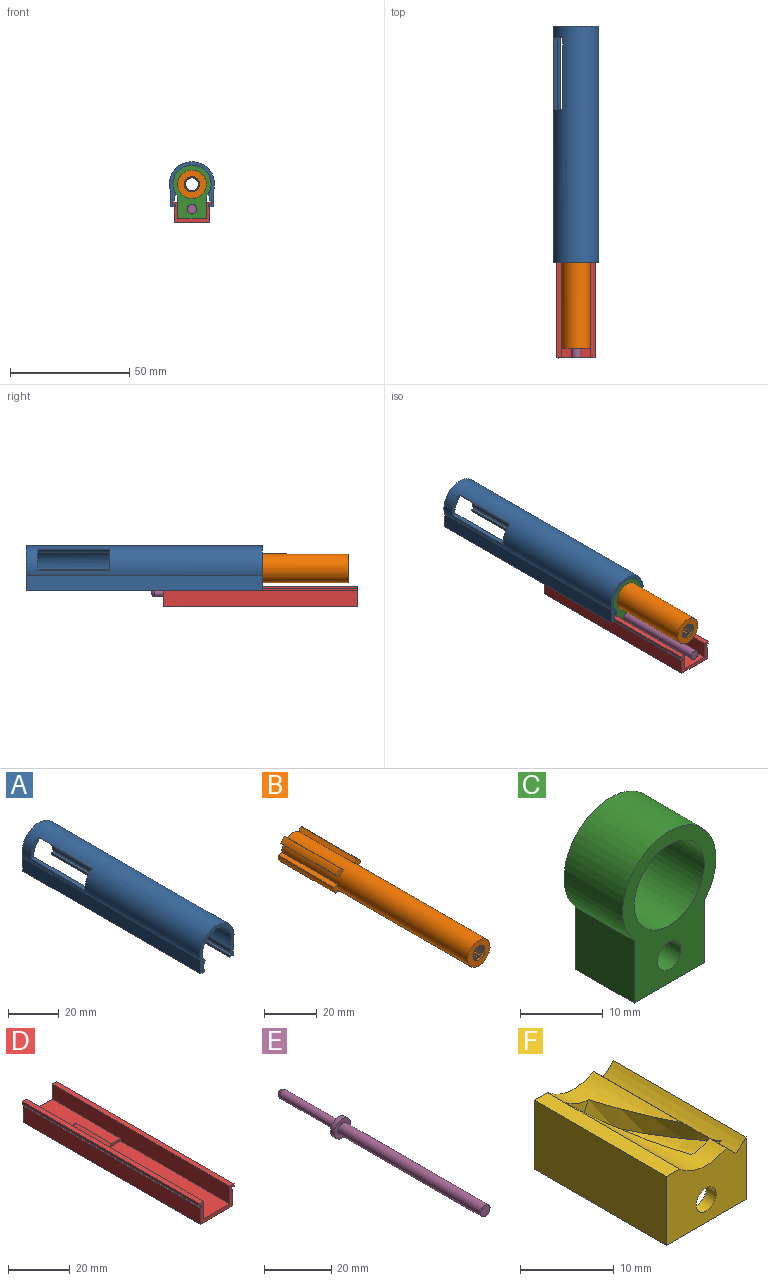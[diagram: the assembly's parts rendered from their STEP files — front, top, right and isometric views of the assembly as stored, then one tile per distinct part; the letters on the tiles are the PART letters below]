
ASSEMBLY  parts=6 mates=6
PART A: 42 faces, bbox 19x99x18.9 mm
  f0: plane 4.17x4.17mm, normal (0,1,0), area 8.4mm2, adj f13,f14,f15,f16
  f1: plane 4.97x2.8mm, normal (0,1,0), area 8.4mm2, adj f16,f17,f18,f19
  f2: plane 12.14x6.49mm, normal (0,1,0), area 30.4mm2, adj f7,f8,f9,f10,f11,f12,f16,f28
  f3: plane 4.97x2.8mm, normal (0,-1,0), area 8.4mm2, adj f7,f8,f9,f16
  f4: plane 4.17x4.17mm, normal (0,-1,0), area 8.4mm2, adj f10,f11,f12,f16
  f5: plane 4.17x4.17mm, normal (0,-1,0), area 8.4mm2, adj f13,f14,f15,f16
  f6: plane 99x1.35mm, normal (0.84,0,-0.54), area 159.4mm2, adj f7,f16,f35,f37,f41
  f7: plane 54x1.45mm, normal (0.71,0,-0.71), area 110.8mm2, adj f2,f3,f6,f8
  f8: cylinder r=5.98mm len=54mm, axis (0,1,0), area 168.9mm2, adj f2,f3,f7,f9
  f9: plane 54x1.98mm, normal (0.26,0,0.97), area 110.8mm2, adj f2,f3,f8,f16
  f10: plane 54x1.98mm, normal (-0.26,0,-0.97), area 110.8mm2, adj f2,f4,f11,f16
  f11: cylinder r=5.98mm len=54mm, axis (0,1,0), area 168.9mm2, adj f2,f4,f10,f12
  f12: plane 54x1.98mm, normal (0.97,0,0.26), area 110.8mm2, adj f2,f4,f11,f16
  f13: plane 54x1.98mm, normal (-0.97,0,0.26), area 110.8mm2, adj f0,f5,f14,f16
  f14: cylinder r=5.98mm len=54mm, axis (0,1,0), area 168.9mm2, adj f0,f5,f13,f15
  f15: plane 54x1.98mm, normal (0.26,0,-0.97), area 110.8mm2, adj f0,f5,f14,f16
  f16: cylinder r=7.97mm len=99mm, axis (0,1,0), area 2030.3mm2, adj f0,f1,f2,f3,f4,f5,f6,f9
  f17: plane 54x1.98mm, normal (-0.26,0,0.97), area 110.8mm2, adj f1,f16,f18,f36
  f18: cylinder r=5.98mm len=54mm, axis (0,1,0), area 168.9mm2, adj f1,f17,f19,f36
  f19: plane 54x1.45mm, normal (-0.71,0,-0.71), area 110.8mm2, adj f1,f18,f20,f36
  f20: plane 99x1.35mm, normal (-0.84,0,-0.54), area 159.4mm2, adj f16,f19,f21,f37,f41
  f21: plane 99x1.65mm, normal (-1,0,0), area 163.2mm2, adj f20,f22,f37,f41
  f22: plane 99x0.5mm, normal (0,0,-1), area 49.5mm2, adj f21,f23,f37,f41
  f23: plane 99x1mm, normal (-1,0,0), area 99mm2, adj f22,f24,f37,f41
  f24: plane 99x1mm, normal (0,0,1), area 99mm2, adj f23,f25,f37,f41
  f25: plane 99x1mm, normal (-1,0,0), area 99mm2, adj f24,f26,f37,f41
  f26: plane 99x2mm, normal (0,0,-1), area 198mm2, adj f25,f27,f37,f41
  f27: plane 99x6.48mm, normal (1,0,0), area 641.1mm2, adj f26,f28,f37,f41
  f28: cylinder r=9.48mm len=99mm, axis (0,1,0), area 3245.8mm2, adj f2,f27,f29,f37,f38,f39,f40,f41
  f29: plane 99x6.48mm, normal (-1,0,0), area 641.1mm2, adj f28,f30,f37,f41
  f30: plane 99x2mm, normal (0,0,-1), area 198mm2, adj f29,f31,f37,f41
  f31: plane 99x1mm, normal (1,0,0), area 99mm2, adj f30,f32,f37,f41
  f32: plane 99x1mm, normal (0,0,1), area 99mm2, adj f31,f33,f37,f41
  f33: plane 99x1mm, normal (1,0,0), area 99mm2, adj f32,f34,f37,f41
  f34: plane 99x0.5mm, normal (0,0,-1), area 49.5mm2, adj f33,f35,f37,f41
  f35: plane 99x1.65mm, normal (1,0,0), area 163.2mm2, adj f6,f34,f37,f41
  f36: plane 4.97x2.8mm, normal (0,-1,0), area 8.4mm2, adj f16,f17,f18,f19
  f37: plane 18.95x18.91mm, normal (0,-1,0), area 72.1mm2, adj f6,f16,f20,f21,f22,f23,f24,f25
  f38: plane 30x1.08mm, normal (-0.71,0,-0.71), area 45.7mm2, adj f2,f16,f28,f40
  f39: plane 30x1.47mm, normal (-0.26,0,0.97), area 45.7mm2, adj f2,f16,f28,f40
  f40: plane 8.63x5.04mm, normal (0,-1,0), area 13.7mm2, adj f16,f28,f38,f39
  f41: plane 18.95x18.91mm, normal (0,1,0), area 72.1mm2, adj f6,f16,f20,f21,f22,f23,f24,f25
PART B: 124 faces, bbox 15.9x105.5x15 mm
  f0: plane 0.75x0.5mm, normal (0,-1,0), area 0.2mm2, adj f45,f48,f55,f102
  f1: plane 0.75x0.66mm, normal (0,1,0), area 0.2mm2, adj f2,f51,f99,f100
  f2: cylinder r=2.85mm len=73.48mm, axis (0,1,0), area 45.5mm2, adj f1,f3,f99,f100
  f3: plane 0.75x0.43mm, normal (0,-1,0), area 0.2mm2, adj f2,f48,f99,f100
  f4: plane 0.75x0.66mm, normal (0,1,0), area 0.2mm2, adj f5,f51,f96,f97
  f5: cylinder r=2.85mm len=73.48mm, axis (0,1,0), area 45.5mm2, adj f4,f6,f96,f97
  f6: plane 0.77x0.64mm, normal (0,-1,0), area 0.2mm2, adj f5,f48,f96,f97
  f7: plane 0.74x0.46mm, normal (0,1,0), area 0.2mm2, adj f8,f51,f93,f94
  f8: cylinder r=2.85mm len=73.48mm, axis (0,1,0), area 45.5mm2, adj f7,f9,f93,f94
  f9: plane 0.76x0.69mm, normal (0,-1,0), area 0.2mm2, adj f8,f48,f93,f94
  f10: plane 0.74x0.46mm, normal (0,1,0), area 0.2mm2, adj f11,f51,f90,f91
  f11: cylinder r=2.85mm len=73.48mm, axis (0,1,0), area 45.5mm2, adj f10,f12,f90,f91
  f12: plane 0.75x0.5mm, normal (0,-1,0), area 0.2mm2, adj f11,f48,f90,f91
  f13: plane 0.75x0.66mm, normal (0,1,0), area 0.2mm2, adj f14,f51,f87,f88
  f14: cylinder r=2.85mm len=73.48mm, axis (0,1,0), area 45.5mm2, adj f13,f15,f87,f88
  f15: plane 0.75x0.43mm, normal (0,-1,0), area 0.2mm2, adj f14,f48,f87,f88
  f16: plane 0.75x0.66mm, normal (0,1,0), area 0.2mm2, adj f17,f51,f84,f85
  f17: cylinder r=2.85mm len=73.48mm, axis (0,1,0), area 45.5mm2, adj f16,f18,f84,f85
  f18: plane 0.77x0.64mm, normal (0,-1,0), area 0.2mm2, adj f17,f48,f84,f85
  f19: plane 0.74x0.46mm, normal (0,1,0), area 0.2mm2, adj f20,f51,f81,f82
  f20: cylinder r=2.85mm len=73.48mm, axis (0,1,0), area 45.5mm2, adj f19,f21,f81,f82
  f21: plane 0.76x0.69mm, normal (0,-1,0), area 0.2mm2, adj f20,f48,f81,f82
  f22: plane 0.74x0.46mm, normal (0,1,0), area 0.2mm2, adj f23,f51,f78,f79
  f23: cylinder r=2.85mm len=73.48mm, axis (0,1,0), area 45.5mm2, adj f22,f24,f78,f79
  f24: plane 0.75x0.5mm, normal (0,-1,0), area 0.2mm2, adj f23,f48,f78,f79
  f25: plane 0.75x0.66mm, normal (0,1,0), area 0.2mm2, adj f26,f51,f75,f76
  f26: cylinder r=2.85mm len=73.48mm, axis (0,1,0), area 45.5mm2, adj f25,f27,f75,f76
  f27: plane 0.75x0.43mm, normal (0,-1,0), area 0.2mm2, adj f26,f48,f75,f76
  f28: plane 0.75x0.66mm, normal (0,1,0), area 0.2mm2, adj f29,f51,f72,f73
  f29: cylinder r=2.85mm len=73.48mm, axis (0,1,0), area 45.5mm2, adj f28,f30,f72,f73
  f30: plane 0.77x0.64mm, normal (0,-1,0), area 0.2mm2, adj f29,f48,f72,f73
  f31: plane 0.74x0.46mm, normal (0,1,0), area 0.2mm2, adj f32,f51,f69,f70
  f32: cylinder r=2.85mm len=73.48mm, axis (0,1,0), area 45.5mm2, adj f31,f33,f69,f70
  f33: plane 0.76x0.69mm, normal (0,-1,0), area 0.2mm2, adj f32,f48,f69,f70
  f34: plane 0.74x0.46mm, normal (0,1,0), area 0.2mm2, adj f35,f51,f66,f67
  f35: cylinder r=2.85mm len=73.48mm, axis (0,1,0), area 45.5mm2, adj f34,f36,f66,f67
  f36: plane 0.76x0.51mm, normal (0,-1,0), area 0.2mm2, adj f35,f48,f66,f67
  f37: plane 0.75x0.66mm, normal (0,1,0), area 0.2mm2, adj f38,f51,f63,f64
  f38: cylinder r=2.85mm len=73.48mm, axis (0,1,0), area 45.5mm2, adj f37,f39,f63,f64
  f39: plane 0.75x0.44mm, normal (0,-1,0), area 0.2mm2, adj f38,f48,f63,f64
  f40: plane 0.75x0.66mm, normal (0,1,0), area 0.2mm2, adj f41,f51,f60,f61
  f41: cylinder r=2.85mm len=73.48mm, axis (0,1,0), area 45.5mm2, adj f40,f42,f60,f61
  f42: plane 0.78x0.65mm, normal (0,-1,0), area 0.2mm2, adj f41,f48,f60,f61
  f43: plane 0.74x0.46mm, normal (0,1,0), area 0.2mm2, adj f44,f51,f57,f58
  f44: cylinder r=2.85mm len=73.48mm, axis (0,1,0), area 45.5mm2, adj f43,f49,f57,f58
  f45: cylinder r=2.85mm len=73.48mm, axis (0,1,0), area 45.5mm2, adj f0,f50,f55,f102
  f46: cylinder r=5.98mm len=100mm, axis (0,1,0), area 3358.4mm2, adj f47,f54,f103,f105,f106,f107,f108,f110
  f47: plane 11.95x11.95mm, normal (0,-1,0), area 80.2mm2, adj f46,f48
  f48: cylinder r=3.19mm len=6.38mm, axis (0,1,0), area 20mm2, adj f0,f3,f6,f9,f12,f15,f18,f21
  f49: plane 0.76x0.69mm, normal (0,-1,0), area 0.2mm2, adj f44,f48,f57,f58
  f50: plane 0.74x0.46mm, normal (0,1,0), area 0.2mm2, adj f45,f51,f55,f102
  f51: cylinder r=3.19mm len=6.38mm, axis (0,1,0), area 92.8mm2, adj f1,f4,f7,f10,f13,f16,f19,f22
  f52: cone r=3.98mm half-angle=35deg, axis (0,1,0), area 30.8mm2, adj f51,f53
  f53: cylinder r=3.98mm len=19.77mm, axis (0,1,0), area 493.8mm2, adj f52,f54
  f54: plane 15.91x12.6mm, normal (0,1,0), area 87.5mm2, adj f46,f53,f103,f104,f105,f107,f108,f109
  f55: bspline ~80.01x4.89mm, area 25.2mm2, adj f0,f45,f50,f56
  f56: bspline ~80.01x5.29mm, area 36.8mm2, adj f48,f51,f55,f57
  f57: bspline ~80.01x5.25mm, area 25.1mm2, adj f43,f44,f49,f56
  f58: bspline ~80.01x5.61mm, area 25mm2, adj f43,f44,f49,f59
  f59: bspline ~80.01x5.88mm, area 36.8mm2, adj f48,f51,f58,f60
  f60: bspline ~80.01x5.68mm, area 25.1mm2, adj f40,f41,f42,f59
  f61: bspline ~80.01x5.53mm, area 25mm2, adj f40,f41,f42,f62
  f62: bspline ~80.01x5.61mm, area 36.8mm2, adj f48,f51,f61,f63
  f63: bspline ~80.01x5.25mm, area 25.2mm2, adj f37,f38,f39,f62
  f64: bspline ~80.01x4.68mm, area 25mm2, adj f37,f38,f39,f65
  f65: bspline ~80.01x4.68mm, area 36.8mm2, adj f48,f51,f64,f66
  f66: bspline ~80.01x4.18mm, area 25.1mm2, adj f34,f35,f36,f65
  f67: bspline ~80.01x4.89mm, area 25mm2, adj f34,f35,f36,f68
  f68: bspline ~80.01x5.29mm, area 36.8mm2, adj f48,f51,f67,f69
  f69: bspline ~80.01x5.25mm, area 25.1mm2, adj f31,f32,f33,f68
  f70: bspline ~80.01x5.61mm, area 25.2mm2, adj f31,f32,f33,f71
  f71: bspline ~80.01x5.88mm, area 36.8mm2, adj f48,f51,f70,f72
  f72: bspline ~80.01x5.68mm, area 25.1mm2, adj f28,f29,f30,f71
  f73: bspline ~80.01x5.53mm, area 25.2mm2, adj f28,f29,f30,f74
  f74: bspline ~80.01x5.61mm, area 36.8mm2, adj f48,f51,f73,f75
  f75: bspline ~80.01x5.25mm, area 25.1mm2, adj f25,f26,f27,f74
  f76: bspline ~80.01x4.68mm, area 25.2mm2, adj f25,f26,f27,f77
  f77: bspline ~80.01x4.68mm, area 36.8mm2, adj f48,f51,f76,f78
  f78: bspline ~80.01x4.18mm, area 25.1mm2, adj f22,f23,f24,f77
  f79: bspline ~80.01x4.89mm, area 25.2mm2, adj f22,f23,f24,f80
  f80: bspline ~80.01x5.29mm, area 36.8mm2, adj f48,f51,f79,f81
  f81: bspline ~80.01x5.25mm, area 25.1mm2, adj f19,f20,f21,f80
  f82: bspline ~80.01x5.61mm, area 25.2mm2, adj f19,f20,f21,f83
  f83: bspline ~80.01x5.88mm, area 36.8mm2, adj f48,f51,f82,f84
  f84: bspline ~80.01x5.68mm, area 25.1mm2, adj f16,f17,f18,f83
  f85: bspline ~80.01x5.53mm, area 25.2mm2, adj f16,f17,f18,f86
  f86: bspline ~80.01x5.61mm, area 36.8mm2, adj f48,f51,f85,f87
  f87: bspline ~80.01x5.25mm, area 25.1mm2, adj f13,f14,f15,f86
  f88: bspline ~80.01x4.68mm, area 25.2mm2, adj f13,f14,f15,f89
  f89: bspline ~80.01x4.68mm, area 36.8mm2, adj f48,f51,f88,f90
  f90: bspline ~80.01x4.18mm, area 25.1mm2, adj f10,f11,f12,f89
  f91: bspline ~80.01x4.89mm, area 25.2mm2, adj f10,f11,f12,f92
  f92: bspline ~80.01x5.29mm, area 36.8mm2, adj f48,f51,f91,f93
  f93: bspline ~80.01x5.25mm, area 25.1mm2, adj f7,f8,f9,f92
  f94: bspline ~80.01x5.61mm, area 25.2mm2, adj f7,f8,f9,f95
  f95: bspline ~80.01x5.88mm, area 36.8mm2, adj f48,f51,f94,f96
  f96: bspline ~80.01x5.68mm, area 25.1mm2, adj f4,f5,f6,f95
  f97: bspline ~80.01x5.53mm, area 25.2mm2, adj f4,f5,f6,f98
  f98: bspline ~80.01x5.61mm, area 36.8mm2, adj f48,f51,f97,f99
  f99: bspline ~80.01x5.25mm, area 25.1mm2, adj f1,f2,f3,f98
  f100: bspline ~80.01x4.68mm, area 25.2mm2, adj f1,f2,f3,f101
  f101: bspline ~80.01x4.68mm, area 36.8mm2, adj f48,f51,f100,f102
  f102: bspline ~80.01x4.18mm, area 25.1mm2, adj f0,f45,f50,f101
  f103: plane 30x1.98mm, normal (0.26,0,-0.97), area 61.6mm2, adj f46,f54,f104,f106
  f104: cylinder r=7.97mm len=30mm, axis (0,1,0), area 93.4mm2, adj f54,f103,f105,f106
  f105: plane 30x1.98mm, normal (-0.26,0,0.97), area 61.6mm2, adj f46,f54,f104,f106
  f106: plane 3.52x2.78mm, normal (0,-1,0), area 6.2mm2, adj f46,f103,f104,f105
  f107: plane 30x1.98mm, normal (-0.26,0,-0.97), area 61.6mm2, adj f46,f54,f109,f110
  f108: plane 30x1.98mm, normal (0.26,0,0.97), area 61.6mm2, adj f46,f54,f109,f110
  f109: cylinder r=7.97mm len=30mm, axis (0,1,0), area 93.4mm2, adj f54,f107,f108,f110
  f110: plane 3.52x2.78mm, normal (0,-1,0), area 6.2mm2, adj f46,f107,f108,f109
  f111: plane 30x1.45mm, normal (0.71,0,-0.71), area 61.6mm2, adj f46,f54,f113,f114
  f112: plane 30x1.45mm, normal (-0.71,0,0.71), area 61.6mm2, adj f46,f54,f113,f114
  f113: cylinder r=7.97mm len=30mm, axis (0,1,0), area 93.4mm2, adj f54,f111,f112,f114
  f114: plane 3.64x3.64mm, normal (0,-1,0), area 6.2mm2, adj f46,f111,f112,f113
  f115: plane 30x1.45mm, normal (0.71,0,0.71), area 61.6mm2, adj f46,f54,f117,f118
  f116: plane 30x1.45mm, normal (-0.71,0,-0.71), area 61.6mm2, adj f46,f54,f117,f118
  f117: cylinder r=7.97mm len=30mm, axis (0,1,0), area 93.4mm2, adj f54,f115,f116,f118
  f118: plane 3.64x3.64mm, normal (0,-1,0), area 6.2mm2, adj f46,f115,f116,f117
  f119: bspline ~5x2.45mm, area 12.5mm2, adj f46,f121,f122,f123
  f120: bspline ~7.5x4.08mm, area 12.5mm2, adj f46,f121,f122,f123
  f121: plane 4.28x2.91mm, normal (0,1,0), area 9.1mm2, adj f46,f119,f120,f123
  f122: plane 4.6x3.71mm, normal (0,-1,0), area 9.1mm2, adj f46,f119,f120,f123
  f123: bspline ~7.5x6.66mm, area 20.2mm2, adj f119,f120,f121,f122
PART C: 10 faces, bbox 16x10x22.4 mm
  f0: plane 10x9.19mm, normal (1,0,0), area 91.8mm2, adj f1,f5,f6,f7
  f1: cylinder r=7.97mm len=15.95mm, axis (0,1,0), area 365.3mm2, adj f0,f2,f6,f7
  f2: plane 10x9.19mm, normal (-1,0,0), area 91.8mm2, adj f1,f5,f6,f7
  f3: cylinder r=5.98mm len=11.95mm, axis (0,1,0), area 375.4mm2, adj f6,f7
  f4: cylinder r=2mm len=5mm, axis (0,1,0), area 62.8mm2, adj f6,f9
  f5: plane 12x10mm, normal (0,0,-1), area 120mm2, adj f0,f2,f6,f7
  f6: plane 22.41x15.95mm, normal (0,-1,0), area 162.7mm2, adj f0,f1,f2,f3,f4,f5
  f7: plane 22.41x15.95mm, normal (0,1,0), area 136.7mm2, adj f0,f1,f2,f3,f5,f8
  f8: cylinder r=3.5mm len=7mm, axis (0,-1,0), area 110mm2, adj f7,f9
  f9: plane 7x7mm, normal (0,1,0), area 25.9mm2, adj f4,f8
PART D: 22 faces, bbox 16x81.5x8.5 mm
  f0: plane 81.5x1mm, normal (0,0,-1), area 81.5mm2, adj f1,f15,f16,f21
  f1: plane 81.5x1mm, normal (-1,0,0), area 81.5mm2, adj f0,f2,f16,f21
  f2: plane 81.5x0.5mm, normal (0,0,1), area 40.7mm2, adj f1,f3,f16,f21
  f3: plane 81.5x6.5mm, normal (-1,0,0), area 529.8mm2, adj f2,f4,f16,f21
  f4: plane 81.5x15mm, normal (0,0,-1), area 1222.5mm2, adj f3,f5,f16,f21
  f5: plane 81.5x6.5mm, normal (1,0,0), area 529.8mm2, adj f4,f6,f16,f21
  f6: plane 81.5x0.5mm, normal (0,0,1), area 40.7mm2, adj f5,f7,f16,f21
  f7: plane 81.5x1mm, normal (1,0,0), area 81.5mm2, adj f6,f8,f16,f21
  f8: plane 81.5x1mm, normal (0,0,-1), area 81.5mm2, adj f7,f9,f16,f21
  f9: plane 81.5x1mm, normal (1,0,0), area 81.5mm2, adj f8,f10,f16,f21
  f10: plane 81.5x2mm, normal (0,0,1), area 163mm2, adj f9,f11,f16,f21
  f11: plane 81.5x7mm, normal (-1,0,0), area 539mm2, adj f10,f12,f16,f17,f19,f21
  f12: plane 50x12mm, normal (0,0,1), area 600mm2, adj f11,f13,f16,f19
  f13: plane 81.5x7mm, normal (1,0,0), area 539mm2, adj f12,f14,f16,f17,f19,f21
  f14: plane 81.5x2mm, normal (0,0,1), area 163mm2, adj f13,f15,f16,f21
  f15: plane 81.5x1mm, normal (-1,0,0), area 81.5mm2, adj f0,f14,f16,f21
  f16: plane 16x8.5mm, normal (0,-1,0), area 43.5mm2, adj f0,f1,f2,f3,f4,f5,f6,f7
  f17: plane 31.5x12mm, normal (0,0,1), area 318.5mm2, adj f11,f13,f18,f19,f20,f21
  f18: cylinder r=3.5mm len=16.5mm, axis (0,-1,0), area 62.5mm2, adj f17,f19,f20
  f19: plane 12x1mm, normal (0,-1,0), area 10.8mm2, adj f11,f12,f13,f17,f18
  f20: plane 3.61x0.5mm, normal (0,-1,0), area 1.2mm2, adj f17,f18
  f21: plane 16x8.5mm, normal (0,1,0), area 55.5mm2, adj f0,f1,f2,f3,f4,f5,f6,f7
PART E: 7 faces, bbox 7x86.5x7 mm
  f0: cylinder r=2mm len=60mm, axis (0,1,0), area 754mm2, adj f1,f4
  f1: plane 4x4mm, normal (0,-1,0), area 12.6mm2, adj f0
  f2: cylinder r=3.5mm len=7mm, axis (0,-1,0), area 33mm2, adj f3,f4
  f3: plane 7x7mm, normal (0,1,0), area 31.4mm2, adj f2,f5
  f4: plane 7x7mm, normal (0,-1,0), area 25.9mm2, adj f0,f2
  f5: cylinder r=1.5mm len=23.5mm, axis (0,-1,0), area 221.5mm2, adj f3,f6
  f6: sphere r=1.5mm, area 14.1mm2, adj f5
PART F: 35 faces, bbox 12x20x9 mm
  f0: plane 12x9mm, normal (0,-1,0), area 88.3mm2, adj f1,f2,f4,f5,f6,f7,f33,f34
  f1: plane 20x12mm, normal (0,0,-1), area 105.7mm2, adj f0,f6,f7,f13,f15,f16,f18,f19
  f2: cylinder r=1.5mm len=3mm, axis (0,1,0), area 14.1mm2, adj f0,f21
  f3: cylinder r=5.98mm len=13.48mm, axis (0,1,0), area 37.6mm2, adj f4,f9,f12,f13,f32
  f4: plane 20x2mm, normal (0,0,1), area 40mm2, adj f0,f3,f5,f7,f8,f12,f13
  f5: cylinder r=5.98mm len=17.49mm, axis (0,1,0), area 53.9mm2, adj f0,f4,f8,f11,f33
  f6: plane 20x8.19mm, normal (1,0,0), area 163.7mm2, adj f0,f1,f13,f34
  f7: plane 20x9mm, normal (-1,0,0), area 180mm2, adj f0,f1,f4,f13
  f8: bspline ~15x6.1mm, area 37.4mm2, adj f4,f5,f10,f11,f12
  f9: bspline ~15x6.1mm, area 32.1mm2, adj f3,f10,f11,f12,f32,f34
  f10: bspline ~15x9.8mm, area 60.6mm2, adj f8,f9,f11,f12
  f11: plane 4.6x2.97mm, normal (0,1,0), area 7.4mm2, adj f5,f8,f9,f10,f33,f34
  f12: plane 4.6x3.7mm, normal (0,-1,0), area 9.1mm2, adj f3,f4,f8,f9,f10
  f13: plane 12x9mm, normal (0,1,0), area 88.3mm2, adj f1,f3,f4,f6,f7,f14,f32,f34
  f14: cylinder r=1.5mm len=3mm, axis (0,1,0), area 14.1mm2, adj f13,f16
  f15: plane 9x4.5mm, normal (0,1,0), area 33.4mm2, adj f1,f17,f18,f19,f20
  f16: plane 5x4.5mm, normal (0,-1,0), area 15.4mm2, adj f1,f14,f17,f26,f27
  f17: plane 9x4.23mm, normal (0,0,-1), area 36.3mm2, adj f15,f16,f18,f19,f26,f27
  f18: plane 4.5x2.23mm, normal (1,0,0), area 10mm2, adj f1,f15,f17,f26
  f19: plane 4.5x2.23mm, normal (-1,0,0), area 10mm2, adj f1,f15,f17,f27
  f20: cylinder r=1.5mm len=3mm, axis (0,1,0), area 14.1mm2, adj f15,f22
  f21: plane 5x4.5mm, normal (0,1,0), area 15.4mm2, adj f1,f2,f23,f28,f31
  f22: plane 5x4.5mm, normal (0,-1,0), area 15.4mm2, adj f1,f20,f23,f29,f30
  f23: plane 11.28x9mm, normal (0,0,-1), area 98mm2, adj f21,f22,f24,f25,f28,f29,f30,f31
  f24: plane 7.28x4.5mm, normal (1,0,0), area 32.7mm2, adj f1,f23,f30,f31
  f25: plane 7.28x4.5mm, normal (-1,0,0), area 32.7mm2, adj f1,f23,f28,f29
  f26: cylinder r=2mm len=4.5mm, axis (0,0,1), area 14.1mm2, adj f1,f16,f17,f18
  f27: cylinder r=2mm len=4.5mm, axis (0,0,-1), area 14.1mm2, adj f1,f16,f17,f19
  f28: cylinder r=2mm len=4.5mm, axis (0,0,1), area 14.1mm2, adj f1,f21,f23,f25
  f29: cylinder r=2mm len=4.5mm, axis (0,0,-1), area 14.1mm2, adj f1,f22,f23,f25
  f30: cylinder r=2mm len=4.5mm, axis (0,0,1), area 14.1mm2, adj f1,f22,f23,f24
  f31: cylinder r=2mm len=4.5mm, axis (0,0,-1), area 14.1mm2, adj f1,f21,f23,f24
  f32: plane 16.44x1.45mm, normal (0.71,0,0.71), area 31mm2, adj f3,f9,f13,f34
  f33: plane 2.5x1.45mm, normal (0.71,0,0.71), area 5.1mm2, adj f0,f5,f11,f34
  f34: cylinder r=7.97mm len=20mm, axis (0,1,0), area 41.5mm2, adj f0,f6,f9,f11,f13,f32,f33
PLACE A t=(12.01,32,-2.64)mm
PLACE B rot(axis=(0,1,0),30deg) t=(12.01,32,-2.64)mm
PLACE C t=(12.01,-22,-2.64)mm
PLACE D t=(12.01,-72,-10.08)mm fixed
PLACE E t=(12.01,-12,-13.08)mm
PLACE F t=(12.01,7,-7.08)mm fixed
MATE fastened A.f8 <-> C.f1  axis (0,-1,0) through (12.01,-32,-2.64)mm
MATE cylindrical B.f2 <-> F.f3  axis (0,1,0) through (12.01,32,-2.64)mm
MATE slider C.f4 <-> E.f0  axis (0,-1,0) through (12.01,-32,-13.08)mm
MATE slider F.f2 <-> E.f5  axis (0,-1,0) through (12.01,-10.5,-13.08)mm
MATE slider D.f16 <-> C.f6  axis (0,-1,0) through (6.01,-72,-17.08)mm
MATE cylindrical B.f2 <-> C.f3  axis (0,-1,0) through (12.01,-68,-2.64)mm
